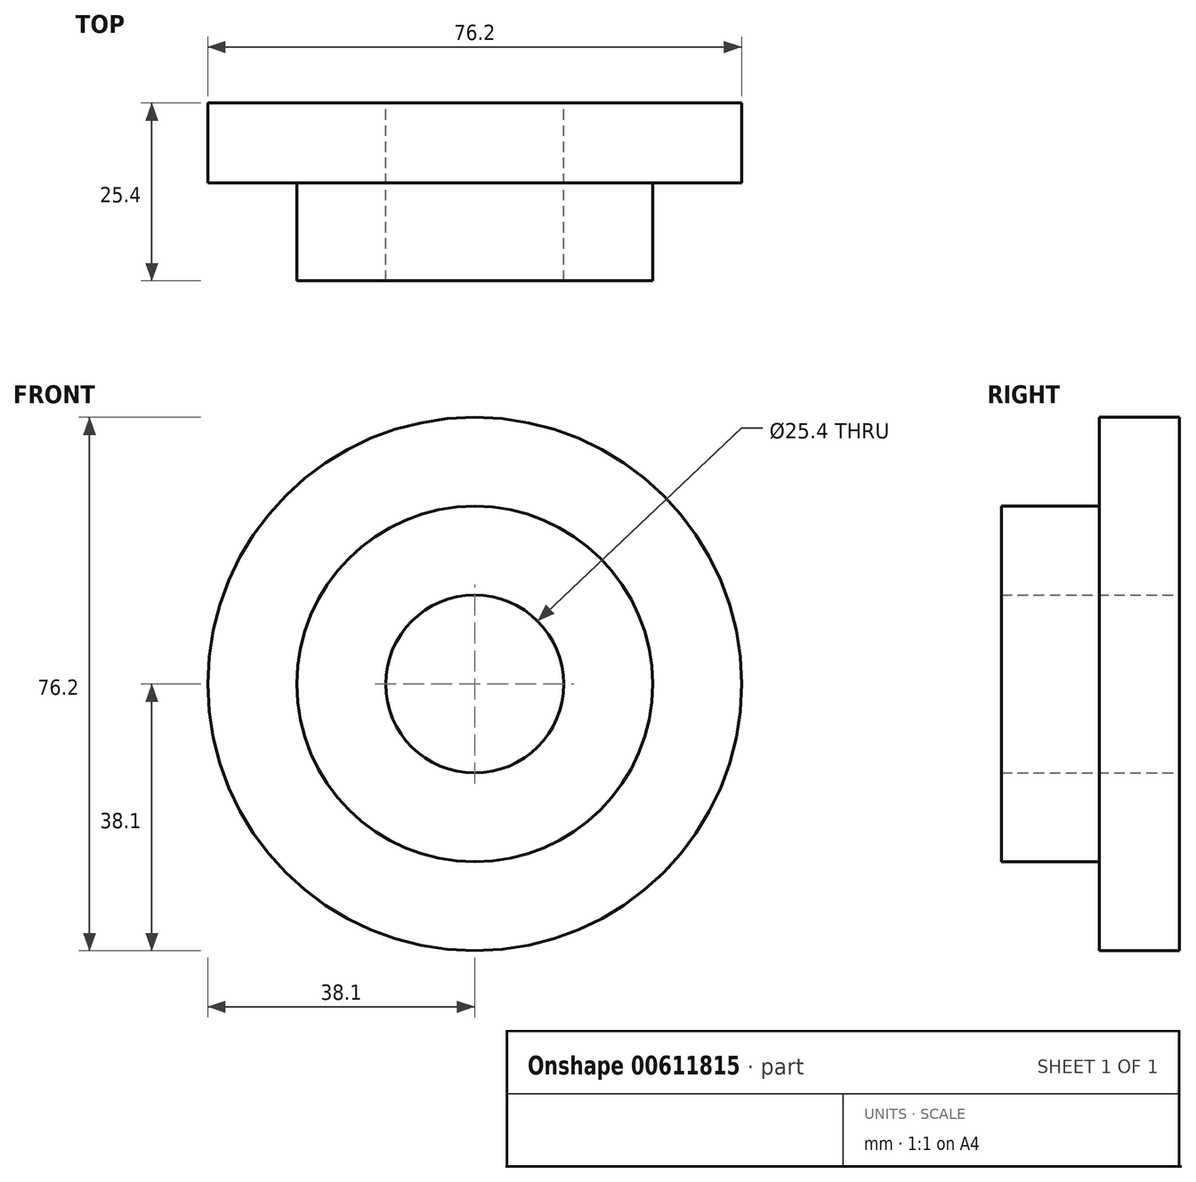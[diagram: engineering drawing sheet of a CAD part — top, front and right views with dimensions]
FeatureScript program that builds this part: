
annotation { "Feature Type Name" : "Feature", "Feature Type Description" : "" }
export const myFeature = defineFeature(function(context is Context, id is Id, definition is map)
    precondition{}
    {
        {
            var Q0;
            Q0=qCreatedBy(makeId("Front.planeOp"),FACE);
            var sketch = newSketch(context, id + "F0", { "sketchPlane" : qUnion([Q0])});
            skCircle(sketch, "E0", {"center": v(0, 0) * mm, "radius": 38.1 * mm});
            skCircle(sketch, "E1", {"center": v(0, 0) * mm, "radius": 12.7 * mm});
            skCircle(sketch, "E2", {"center": v(0, 0) * mm, "radius": 25.4 * mm});
            skSolve(sketch);
        }
        {
            var Q0;
            Q0 = qSketchRegion(id + "F0", true);
            extrude(context, id + "F1", {"entities" : qUnion([Q0]), "depth" : 11.43 * mm, "offsetDistance" : 25.4 * mm});
        }
        {
            var Q0;
            Q0=makeQuery(id+"F0.imprint","IMPRINT",FACE,{"disambiguationData":[TD([[makeQuery(id+"F0.imprint","IMPRINT",EDGE,{"derivedFrom":sQuery(id+"F0.wireOp",EDGE,"E1")}),-1.0]])]});
            extrude(context, id + "F2", {"entities" : qUnion([Q0]), "operationType" : NewBodyOperationType.ADD, "depth" : 25.4 * mm, "offsetDistance" : 25.4 * mm});
        }
    });
